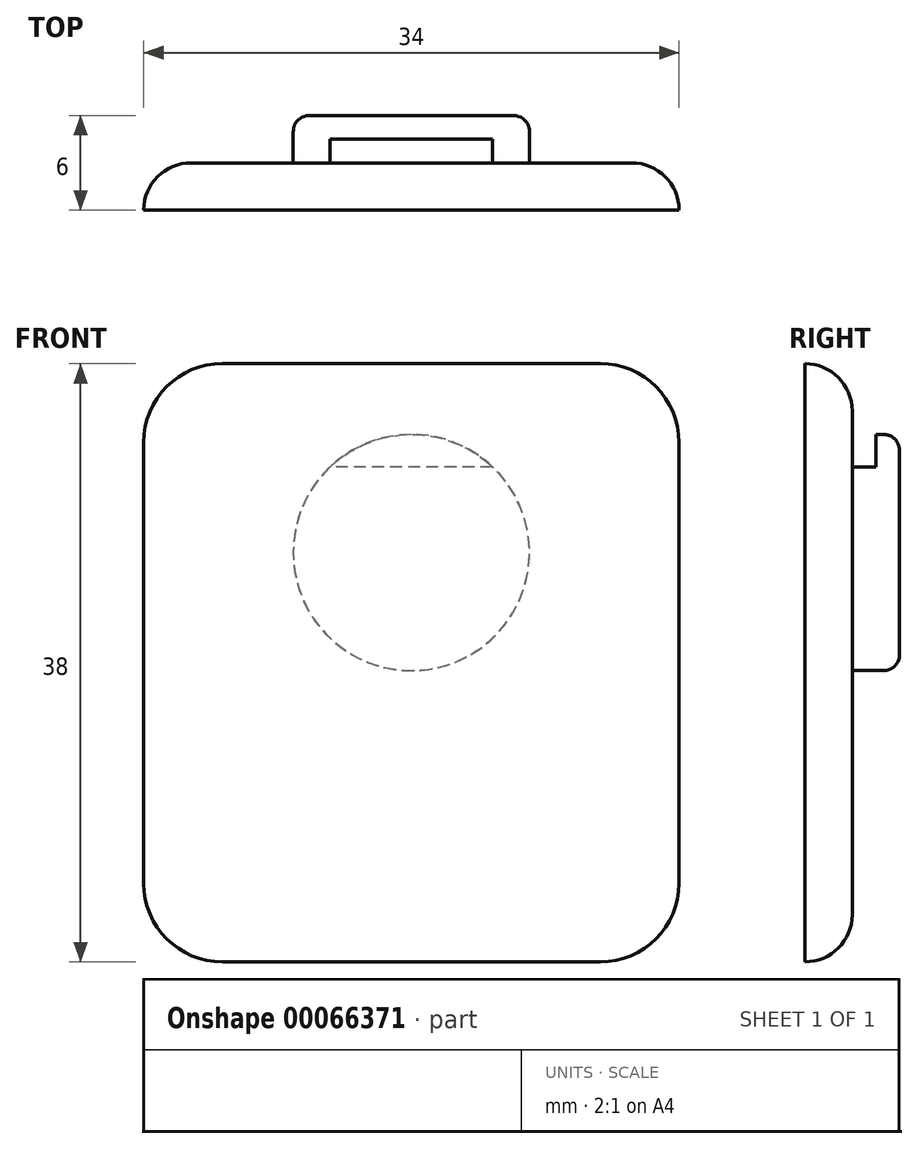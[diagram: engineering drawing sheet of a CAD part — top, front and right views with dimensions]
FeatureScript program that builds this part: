
annotation { "Feature Type Name" : "Feature", "Feature Type Description" : "" }
export const myFeature = defineFeature(function(context is Context, id is Id, definition is map)
    precondition{}
    {
        {
            var Q0;
            Q0=qCreatedBy(makeId("Front.planeOp"),FACE);
            var sketch = newSketch(context, id + "F0", { "sketchPlane" : qUnion([Q0])});
            skLineSegment(sketch, "E0", {"start": v(-12, 0) * mm, "end": v(12, 0) * mm});
            skLineSegment(sketch, "E1", {"start": v(17, 5) * mm, "end": v(17, 33) * mm});
            skLineSegment(sketch, "E2", {"start": v(12, 38) * mm, "end": v(-12, 38) * mm});
            skLineSegment(sketch, "E3", {"start": v(-17, 33) * mm, "end": v(-17, 5) * mm});
            skPoint(sketch, "E4.visualSharp", {"position": v(-17, 38) * mm});
            skArc(sketch, "E4.filletArc", {"start": v(-12, 38) * mm, "mid": v(-15.54, 36.54) * mm, "end": v(-17, 33) * mm});
            skPoint(sketch, "E5.visualSharp", {"position": v(-17, 0) * mm});
            skArc(sketch, "E5.filletArc", {"start": v(-17, 5) * mm, "mid": v(-15.54, 1.46) * mm, "end": v(-12, 0) * mm});
            skPoint(sketch, "E6.visualSharp", {"position": v(17, 0) * mm});
            skArc(sketch, "E6.filletArc", {"start": v(12, 0) * mm, "mid": v(15.54, 1.46) * mm, "end": v(17, 5) * mm});
            skPoint(sketch, "E7.visualSharp", {"position": v(17, 38) * mm});
            skArc(sketch, "E7.filletArc", {"start": v(17, 33) * mm, "mid": v(15.54, 36.54) * mm, "end": v(12, 38) * mm});
            skSolve(sketch);
        }
        {
            var Q0;
            Q0=makeQuery(id+"F0.imprint","IMPRINT",FACE,{"disambiguationData":[TD([[makeQuery(id+"F0.imprint","IMPRINT",EDGE,{"derivedFrom":sQuery(id+"F0.wireOp",EDGE,"E0")}),1.0]])]});
            extrude(context, id + "F1", {"entities" : qUnion([Q0]), "depth" : 3 * mm});
        }
        {
            var Q0;
            Q0=makeQuery(id+"F1.opExtrude","CAP_FACE",FACE,{"disambiguationData":[OSD([sQuery(id+"F0.wireOp",EDGE,"E0"),sQuery(id+"F0.wireOp",EDGE,"E1"),sQuery(id+"F0.wireOp",EDGE,"E2"),sQuery(id+"F0.wireOp",EDGE,"E3"),sQuery(id+"F0.wireOp",EDGE,"E4.filletArc"),sQuery(id+"F0.wireOp",EDGE,"E5.filletArc"),sQuery(id+"F0.wireOp",EDGE,"E6.filletArc"),sQuery(id+"F0.wireOp",EDGE,"E7.filletArc")])],"isStart":true});
            var sketch = newSketch(context, id + "F2", { "sketchPlane" : qUnion([Q0])});
            skCircle(sketch, "E8", {"center": v(0, 26) * mm, "radius": 7.5 * mm});
            skSolve(sketch);
        }
        {
            var Q0;
            Q0 = qSketchRegion(id + "F2", true);
            extrude(context, id + "F3", {"entities" : qUnion([Q0]), "operationType" : NewBodyOperationType.ADD, "depth" : 3 * mm});
        }
        {
            var Q0;
            Q0=qCreatedBy(makeId("Right.planeOp"),FACE);
            var sketch = newSketch(context, id + "F4", { "sketchPlane" : qUnion([Q0])});
            skLineSegment(sketch, "E9", {"start": v(0, 33.5) * mm, "end": v(2.84, 33.5) * mm});
            skLineSegment(sketch, "E10", {"start": v(1.5, 33.5) * mm, "end": v(1.5, 31.45) * mm});
            skLineSegment(sketch, "E11", {"start": v(1.5, 33.5) * mm, "end": v(0, 33.5) * mm});
            skLineSegment(sketch, "E12", {"start": v(1.5, 31.45) * mm, "end": v(0, 31.45) * mm});
            skLineSegment(sketch, "E13", {"start": v(0, 31.45) * mm, "end": v(0, 33.5) * mm});
            skSolve(sketch);
        }
        {
            var Q0;
            Q0 = qSketchRegion(id + "F4", true);
            extrude(context, id + "F5", {"entities" : qUnion([Q0]), "operationType" : NewBodyOperationType.REMOVE, "depth" : 25 * mm, "symmetric" : true});
        }
        {
            var Q0;
            Q0=makeQuery(id+"F1.opExtrude","CAP_EDGE",EDGE,{"disambiguationData":[OSD([sQuery(id+"F0.wireOp",EDGE,"E1")])],"isStart":true});
            fillet(context, id + "F6", {"entities" : qUnion([Q0]), "radius" : 3 * mm, "tangentPropagation" : true, "allowEdgeOverflow" : false});
        }
        {
            var Q0;
            Q0=makeQuery(id+"F3.opExtrude","CAP_EDGE",EDGE,{"disambiguationData":[OSD([sQuery(id+"F2.wireOp",EDGE,"E8")])],"isStart":false});
            var Q1;
            Q1=makeQuery(id+"F3.opExtrude","CAP_EDGE",EDGE,{"disambiguationData":[OSD([sQuery(id+"F2.wireOp",EDGE,"E8")])],"isStart":true});
            fillet(context, id + "F7", {"entities" : qUnion([Q0, Q1]), "radius" : 1 * mm, "tangentPropagation" : true, "allowEdgeOverflow" : false});
        }
    });
